# Revit family: QF_Kelvinator_738282_KCHRI54R4HDR
name_source: partatom
category: Specialty Equipment
units: mm (PartAtom-declared; Revit-internal decimal feet)

## family parameters
Always vertical = Yes
Cut with Voids When Loaded = No
Part Type = Normal
Room Calculation Point = No
Round Connector Dimension = Use Diameter
Shared = No
Work Plane-Based = No

## types (1)
- QF_Kelvinator_738282_KCHRI54R4HDR
    Accessory = No
    Apparent Power = 0 VA
    Conn Conduit = Yes
    Conn Plug = 5-15P
    Cycle = 60 Hz
    Default Elevation = 0"
    Depth = 32 11/16"
    Depth Actual = 830"
    Description = 4-HALF DOOR FULL HEIGHT REFRIGERATOR 54" LONG
    Elec Conn Connection Height = 0"
    Elec Conn RI Height = 0"
    FL Amps = 5 A
    Foodservice Equipment Identifier = Yes
    Gas KW = 0
    HP = 0.6 HP
    Height = 83"
    Height Actual = 2108"
    Identify Quantity as Lot = Yes
    Item Number = 738282
    Length = 53 15/16"
    Length Actual = 1370"
    Manufacturer = Kelvinator
    Max Overcurrent Protection = 0 A
    Min Ckt Ampacity = 0 A
    Model = KCHRI54R4HDR
    Number of Poles = 1
    Phase = 1
    Refrigerant Type = R290
    URL = KELVINATOR
    URL Manufacturer = KELVINATOR
    Volts = 115 V
    Watts = 0 W
    Weight = 194.00 lbm
    Weight in Pounds = 427.697

## geometry (parser evidence)
native form markers: Sweep x19
no freeform markers — native parametric forms only
